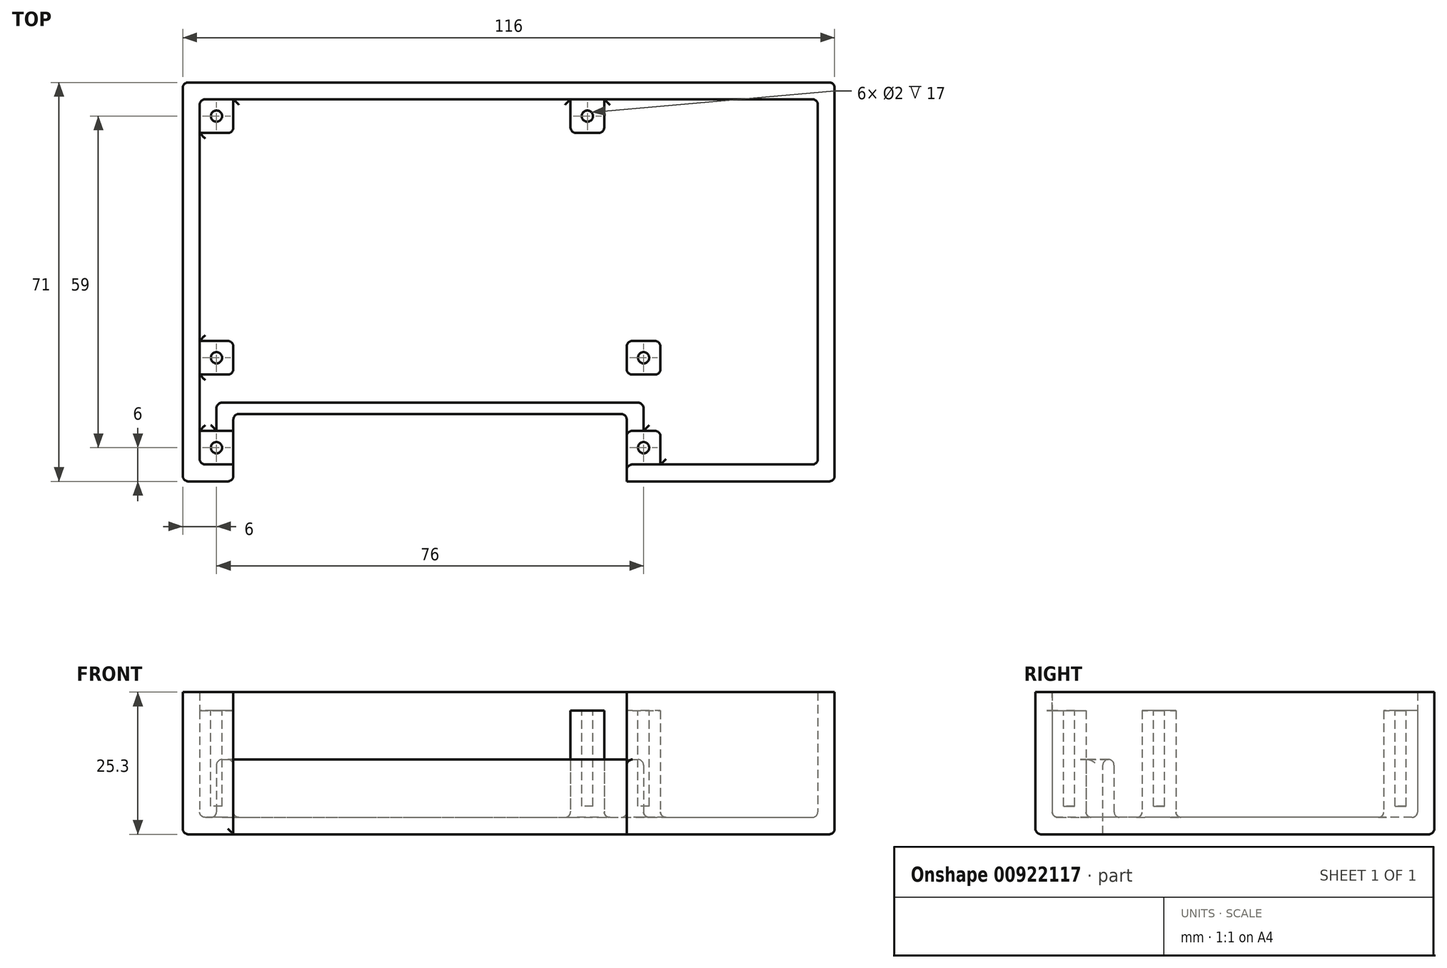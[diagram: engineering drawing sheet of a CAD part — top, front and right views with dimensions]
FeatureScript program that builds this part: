
annotation { "Feature Type Name" : "Feature", "Feature Type Description" : "" }
export const myFeature = defineFeature(function(context is Context, id is Id, definition is map)
    precondition{}
    {
        {
            var Q0;
            Q0=qCreatedBy(makeId("Top.planeOp"),FACE);
            var sketch = newSketch(context, id + "F0", { "sketchPlane" : qUnion([Q0])});
            skLineSegment(sketch, "E0.bottom", {"start": v(58, -35.5) * mm, "end": v(-58, -35.5) * mm});
            skLineSegment(sketch, "E0.top", {"start": v(58, 35.5) * mm, "end": v(-58, 35.5) * mm});
            skLineSegment(sketch, "E0.left", {"start": v(58, -35.5) * mm, "end": v(58, 35.5) * mm});
            skLineSegment(sketch, "E0.right", {"start": v(-58, -35.5) * mm, "end": v(-58, 35.5) * mm});
            skSolve(sketch);
        }
        {
            var Q0;
            Q0 = qSketchRegion(id + "F0", true);
            extrude(context, id + "F1", {"entities" : qUnion([Q0]), "depth" : 3 * mm, "offsetDistance" : 25 * mm});
        }
        {
            var Q0;
            Q0=makeQuery(id+"F1.opExtrude","CAP_FACE",FACE,{"disambiguationData":[OSD([sQuery(id+"F0.wireOp",EDGE,"E0.bottom"),sQuery(id+"F0.wireOp",EDGE,"E0.top"),sQuery(id+"F0.wireOp",EDGE,"E0.left"),sQuery(id+"F0.wireOp",EDGE,"E0.right")])],"isStart":false});
            var sketch = newSketch(context, id + "F2", { "sketchPlane" : qUnion([Q0])});
            skLineSegment(sketch, "E1.bottom", {"start": v(-58, 35.5) * mm, "end": v(58, 35.5) * mm});
            skLineSegment(sketch, "E1.top", {"start": v(-58, -35.5) * mm, "end": v(58, -35.5) * mm});
            skLineSegment(sketch, "E1.left", {"start": v(-58, 35.5) * mm, "end": v(-58, -35.5) * mm});
            skLineSegment(sketch, "E1.right", {"start": v(58, 35.5) * mm, "end": v(58, -35.5) * mm});
            skSolve(sketch);
        }
        {
            var Q0;
            Q0 = qSketchRegion(id + "F2", true);
            extrude(context, id + "F3", {"entities" : qUnion([Q0]), "depth" : 22.3 * mm, "offsetDistance" : 25 * mm});
        }
        {
            var Q0;
            Q0=makeQuery(id+"F1.opExtrude","CAP_FACE",FACE,{"disambiguationData":[OSD([sQuery(id+"F0.wireOp",EDGE,"E0.bottom"),sQuery(id+"F0.wireOp",EDGE,"E0.top"),sQuery(id+"F0.wireOp",EDGE,"E0.left"),sQuery(id+"F0.wireOp",EDGE,"E0.right")])],"isStart":false});
            var sketch = newSketch(context, id + "F4", { "sketchPlane" : qUnion([Q0])});
            skLineSegment(sketch, "E2.bottom", {"start": v(-55, 32.5) * mm, "end": v(55, 32.5) * mm});
            skLineSegment(sketch, "E2.top", {"start": v(-55, -32.5) * mm, "end": v(55, -32.5) * mm});
            skLineSegment(sketch, "E2.left", {"start": v(-55, 32.5) * mm, "end": v(-55, -32.5) * mm});
            skLineSegment(sketch, "E2.right", {"start": v(55, 32.5) * mm, "end": v(55, -32.5) * mm});
            skSolve(sketch);
        }
        {
            var Q0;
            Q0 = qSketchRegion(id + "F4", true);
            extrude(context, id + "F5", {"entities" : qUnion([Q0]), "operationType" : NewBodyOperationType.REMOVE, "depth" : 23 * mm, "offsetDistance" : 25 * mm});
        }
        {
            var Q0;
            Q0=makeQuery(id+"F1.opExtrude","CAP_FACE",FACE,{"disambiguationData":[OSD([sQuery(id+"F0.wireOp",EDGE,"E0.bottom"),sQuery(id+"F0.wireOp",EDGE,"E0.top"),sQuery(id+"F0.wireOp",EDGE,"E0.left"),sQuery(id+"F0.wireOp",EDGE,"E0.right")])],"isStart":false});
            var sketch = newSketch(context, id + "F6", { "sketchPlane" : qUnion([Q0])});
            skLineSegment(sketch, "E3", {"start": v(3.6, 8.06) * mm, "end": v(5.25, 13.83) * mm, "construction": true});
            skLineSegment(sketch, "E4.bottom", {"start": v(-55, -32.5) * mm, "end": v(-49, -32.5) * mm});
            skLineSegment(sketch, "E4.top", {"start": v(-55, -26.5) * mm, "end": v(-49, -26.5) * mm});
            skLineSegment(sketch, "E4.left", {"start": v(-55, -32.5) * mm, "end": v(-55, -26.5) * mm});
            skLineSegment(sketch, "E4.right", {"start": v(-49, -32.5) * mm, "end": v(-49, -26.5) * mm});
            skLineSegment(sketch, "E5.bottom", {"start": v(21, -32.5) * mm, "end": v(27, -32.5) * mm});
            skLineSegment(sketch, "E5.top", {"start": v(21, -26.5) * mm, "end": v(27, -26.5) * mm});
            skLineSegment(sketch, "E5.left", {"start": v(21, -32.5) * mm, "end": v(21, -26.5) * mm});
            skLineSegment(sketch, "E5.right", {"start": v(27, -32.5) * mm, "end": v(27, -26.5) * mm});
            skLineSegment(sketch, "E6.bottom", {"start": v(-49, -10.5) * mm, "end": v(-55, -10.5) * mm});
            skLineSegment(sketch, "E6.top", {"start": v(-49, -16.5) * mm, "end": v(-55, -16.5) * mm});
            skLineSegment(sketch, "E6.left", {"start": v(-49, -10.5) * mm, "end": v(-49, -16.5) * mm});
            skLineSegment(sketch, "E6.right", {"start": v(-55, -10.5) * mm, "end": v(-55, -16.5) * mm});
            skLineSegment(sketch, "E7.bottom", {"start": v(27, -10.5) * mm, "end": v(21, -10.5) * mm});
            skLineSegment(sketch, "E7.top", {"start": v(27, -16.5) * mm, "end": v(21, -16.5) * mm});
            skLineSegment(sketch, "E7.left", {"start": v(27, -10.5) * mm, "end": v(27, -16.5) * mm});
            skLineSegment(sketch, "E7.right", {"start": v(21, -10.5) * mm, "end": v(21, -16.5) * mm});
            skLineSegment(sketch, "E8", {"start": v(21, -10.5) * mm, "end": v(27, -16.5) * mm, "construction": true});
            skPoint(sketch, "E9", {"position": v(24, -13.5) * mm});
            skLineSegment(sketch, "E10", {"start": v(27, -26.5) * mm, "end": v(21, -32.5) * mm, "construction": true});
            skLineSegment(sketch, "E11", {"start": v(-49, -16.5) * mm, "end": v(-55, -10.5) * mm, "construction": true});
            skLineSegment(sketch, "E12", {"start": v(-55, -32.5) * mm, "end": v(-49, -26.5) * mm, "construction": true});
            skPoint(sketch, "E13", {"position": v(-52, -13.5) * mm});
            skPoint(sketch, "E14", {"position": v(-52, -29.5) * mm});
            skPoint(sketch, "E15", {"position": v(24, -29.5) * mm});
            skLineSegment(sketch, "E16", {"start": v(24, -13.5) * mm, "end": v(24, -29.5) * mm, "construction": true});
            skLineSegment(sketch, "E17", {"start": v(24, -13.5) * mm, "end": v(-52, -13.5) * mm, "construction": true});
            skLineSegment(sketch, "E18.bottom", {"start": v(17, 32.5) * mm, "end": v(11, 32.5) * mm});
            skLineSegment(sketch, "E18.top", {"start": v(17, 26.5) * mm, "end": v(11, 26.5) * mm});
            skLineSegment(sketch, "E18.left", {"start": v(17, 32.5) * mm, "end": v(17, 26.5) * mm});
            skLineSegment(sketch, "E18.right", {"start": v(11, 32.5) * mm, "end": v(11, 26.5) * mm});
            skLineSegment(sketch, "E19.bottom", {"start": v(-49, 32.5) * mm, "end": v(-55, 32.5) * mm});
            skLineSegment(sketch, "E19.top", {"start": v(-49, 26.5) * mm, "end": v(-55, 26.5) * mm});
            skLineSegment(sketch, "E19.left", {"start": v(-49, 32.5) * mm, "end": v(-49, 26.5) * mm});
            skLineSegment(sketch, "E19.right", {"start": v(-55, 32.5) * mm, "end": v(-55, 26.5) * mm});
            skLineSegment(sketch, "E20", {"start": v(17, 32.5) * mm, "end": v(11, 26.5) * mm, "construction": true});
            skLineSegment(sketch, "E21", {"start": v(-49, 32.5) * mm, "end": v(-55, 26.5) * mm, "construction": true});
            skPoint(sketch, "E22", {"position": v(-52, 29.5) * mm});
            skPoint(sketch, "E23", {"position": v(14, 29.5) * mm});
            skSolve(sketch);
        }
        {
            var Q0;
            Q0 = qSketchRegion(id + "F6", true);
            extrude(context, id + "F7", {"entities" : qUnion([Q0]), "depth" : 19 * mm, "offsetDistance" : 25 * mm});
        }
        {
            var Q0;
            Q0=makeQuery(id+"F3.opExtrude","CAP_FACE",FACE,{"disambiguationData":[OSD([sQuery(id+"F2.wireOp",EDGE,"E1.bottom"),sQuery(id+"F2.wireOp",EDGE,"E1.top"),sQuery(id+"F2.wireOp",EDGE,"E1.left"),sQuery(id+"F2.wireOp",EDGE,"E1.right")])],"isStart":false});
            var sketch = newSketch(context, id + "F8", { "sketchPlane" : qUnion([Q0])});
            skLineSegment(sketch, "E24.bottom", {"start": v(21, -35.5) * mm, "end": v(-49, -35.5) * mm});
            skLineSegment(sketch, "E24.top", {"start": v(21, -32.5) * mm, "end": v(-49, -32.5) * mm});
            skLineSegment(sketch, "E24.left", {"start": v(21, -35.5) * mm, "end": v(21, -32.5) * mm});
            skLineSegment(sketch, "E24.right", {"start": v(-49, -35.5) * mm, "end": v(-49, -32.5) * mm});
            skSolve(sketch);
        }
        {
            var Q0;
            Q0 = qSketchRegion(id + "F8", true);
            extrude(context, id + "F9", {"entities" : qUnion([Q0]), "operationType" : NewBodyOperationType.REMOVE, "oppositeDirection" : true, "depth" : 24 * mm, "offsetDistance" : 25 * mm});
        }
        {
            var Q0;
            Q0=makeQuery(id+"F7.opExtrude","CAP_FACE",FACE,{"disambiguationData":[OSD([sQuery(id+"F6.wireOp",EDGE,"E4.bottom"),sQuery(id+"F6.wireOp",EDGE,"E4.top"),sQuery(id+"F6.wireOp",EDGE,"E4.left"),sQuery(id+"F6.wireOp",EDGE,"E4.right")])],"isStart":false});
            var sketch = newSketch(context, id + "F10", { "sketchPlane" : qUnion([Q0])});
            skCircle(sketch, "E25", {"center": v(-52, -29.5) * mm, "radius": 1 * mm});
            skCircle(sketch, "E26", {"center": v(-52, -13.5) * mm, "radius": 1 * mm});
            skCircle(sketch, "E27", {"center": v(-52, 29.5) * mm, "radius": 1 * mm});
            skCircle(sketch, "E28", {"center": v(14, 29.5) * mm, "radius": 1 * mm});
            skCircle(sketch, "E29", {"center": v(24, -13.5) * mm, "radius": 1 * mm});
            skCircle(sketch, "E30", {"center": v(24, -29.5) * mm, "radius": 1 * mm});
            skSolve(sketch);
        }
        {
            var Q0;
            Q0 = qSketchRegion(id + "F10", true);
            extrude(context, id + "F11", {"entities" : qUnion([Q0]), "operationType" : NewBodyOperationType.REMOVE, "oppositeDirection" : true, "depth" : 17 * mm, "offsetDistance" : 25 * mm});
        }
        {
            var Q0;
            Q0=makeQuery(id+"F1.opExtrude","CAP_FACE",FACE,{"disambiguationData":[OSD([sQuery(id+"F0.wireOp",EDGE,"E0.bottom"),sQuery(id+"F0.wireOp",EDGE,"E0.top"),sQuery(id+"F0.wireOp",EDGE,"E0.left"),sQuery(id+"F0.wireOp",EDGE,"E0.right")])],"isStart":false});
            var sketch = newSketch(context, id + "F12", { "sketchPlane" : qUnion([Q0])});
            skLineSegment(sketch, "E31.bottom", {"start": v(-52, -21.5) * mm, "end": v(24, -21.5) * mm});
            skLineSegment(sketch, "E31.top", {"start": v(-52, -26.5) * mm, "end": v(24, -26.5) * mm});
            skLineSegment(sketch, "E31.left", {"start": v(-52, -21.5) * mm, "end": v(-52, -26.5) * mm});
            skLineSegment(sketch, "E31.right", {"start": v(24, -21.5) * mm, "end": v(24, -26.5) * mm});
            skSolve(sketch);
        }
        {
            var Q0;
            Q0 = qSketchRegion(id + "F12", true);
            extrude(context, id + "F13", {"entities" : qUnion([Q0]), "depth" : 10.3 * mm, "offsetDistance" : 25 * mm});
        }
        {
            var Q0;
            Q0=makeQuery(id+"F1.opExtrude","CAP_FACE",FACE,{"disambiguationData":[OSD([sQuery(id+"F0.wireOp",EDGE,"E0.bottom"),sQuery(id+"F0.wireOp",EDGE,"E0.top"),sQuery(id+"F0.wireOp",EDGE,"E0.left"),sQuery(id+"F0.wireOp",EDGE,"E0.right")])],"isStart":false});
            var sketch = newSketch(context, id + "F14", { "sketchPlane" : qUnion([Q0])});
            skLineSegment(sketch, "E32.bottom", {"start": v(-49, -35.5) * mm, "end": v(21, -35.5) * mm});
            skLineSegment(sketch, "E32.top", {"start": v(-49, -23.5) * mm, "end": v(21, -23.5) * mm});
            skLineSegment(sketch, "E32.left", {"start": v(-49, -35.5) * mm, "end": v(-49, -23.5) * mm});
            skLineSegment(sketch, "E32.right", {"start": v(21, -35.5) * mm, "end": v(21, -23.5) * mm});
            skLineSegment(sketch, "E33", {"start": v(-52, -29.5) * mm, "end": v(24, -29.5) * mm, "construction": true});
            skSolve(sketch);
        }
        {
            var Q0;
            Q0 = qSketchRegion(id + "F14", true);
            extrude(context, id + "F15", {"entities" : qUnion([Q0]), "operationType" : NewBodyOperationType.REMOVE, "oppositeDirection" : true, "depth" : 3 * mm, "offsetDistance" : 25 * mm, "hasSecondDirection" : true, "secondDirectionOppositeDirection" : false, "secondDirectionDepth" : 11.3 * mm});
        }
        {
            var Q0;
            Q0=makeQuery(id+"F3.opExtrude","SWEPT_BODY",BODY,{"disambiguationData":[OSD([sQuery(id+"F2.wireOp",EDGE,"E1.bottom"),sQuery(id+"F2.wireOp",EDGE,"E1.top"),sQuery(id+"F2.wireOp",EDGE,"E1.left"),sQuery(id+"F2.wireOp",EDGE,"E1.right")])]});
            var Q1;
            Q1=makeQuery(id+"F7.opExtrude","SWEPT_BODY",BODY,{"disambiguationData":[OSD([sQuery(id+"F6.wireOp",EDGE,"E4.bottom"),sQuery(id+"F6.wireOp",EDGE,"E4.top"),sQuery(id+"F6.wireOp",EDGE,"E4.left"),sQuery(id+"F6.wireOp",EDGE,"E4.right")])]});
            var Q2;
            Q2=makeQuery(id+"F7.opExtrude","SWEPT_BODY",BODY,{"disambiguationData":[OSD([sQuery(id+"F6.wireOp",EDGE,"E5.bottom"),sQuery(id+"F6.wireOp",EDGE,"E5.top"),sQuery(id+"F6.wireOp",EDGE,"E5.left"),sQuery(id+"F6.wireOp",EDGE,"E5.right")])]});
            var Q3;
            Q3=makeQuery(id+"F7.opExtrude","SWEPT_BODY",BODY,{"disambiguationData":[OSD([sQuery(id+"F6.wireOp",EDGE,"E6.bottom"),sQuery(id+"F6.wireOp",EDGE,"E6.top"),sQuery(id+"F6.wireOp",EDGE,"E6.left"),sQuery(id+"F6.wireOp",EDGE,"E6.right")])]});
            var Q4;
            Q4=makeQuery(id+"F7.opExtrude","SWEPT_BODY",BODY,{"disambiguationData":[OSD([sQuery(id+"F6.wireOp",EDGE,"E7.bottom"),sQuery(id+"F6.wireOp",EDGE,"E7.top"),sQuery(id+"F6.wireOp",EDGE,"E7.left"),sQuery(id+"F6.wireOp",EDGE,"E7.right")])]});
            var Q5;
            Q5=makeQuery(id+"F7.opExtrude","SWEPT_BODY",BODY,{"disambiguationData":[OSD([sQuery(id+"F6.wireOp",EDGE,"E18.bottom"),sQuery(id+"F6.wireOp",EDGE,"E18.top"),sQuery(id+"F6.wireOp",EDGE,"E18.left"),sQuery(id+"F6.wireOp",EDGE,"E18.right")])]});
            var Q6;
            Q6=makeQuery(id+"F7.opExtrude","SWEPT_BODY",BODY,{"disambiguationData":[OSD([sQuery(id+"F6.wireOp",EDGE,"E19.bottom"),sQuery(id+"F6.wireOp",EDGE,"E19.top"),sQuery(id+"F6.wireOp",EDGE,"E19.left"),sQuery(id+"F6.wireOp",EDGE,"E19.right")])]});
            var Q7;
            Q7=makeQuery(id+"F13.opExtrude","SWEPT_BODY",BODY,{"disambiguationData":[OSD([sQuery(id+"F12.wireOp",EDGE,"E31.bottom"),sQuery(id+"F12.wireOp",EDGE,"E31.top"),sQuery(id+"F12.wireOp",EDGE,"E31.left"),sQuery(id+"F12.wireOp",EDGE,"E31.right")])]});
            var Q8;
            Q8=makeQuery(id+"F1.opExtrude","SWEPT_BODY",BODY,{"disambiguationData":[OSD([sQuery(id+"F0.wireOp",EDGE,"E0.bottom"),sQuery(id+"F0.wireOp",EDGE,"E0.top"),sQuery(id+"F0.wireOp",EDGE,"E0.left"),sQuery(id+"F0.wireOp",EDGE,"E0.right")])]});
            booleanBodies(context, id + "F16", {"operationType" : BooleanOperationType.UNION, "tools" : qUnion([Q0, Q1, Q2, Q3, Q4, Q5, Q6, Q7, Q8])});
        }
        {
            var Q0;
            Q0=makeQuery(id+"F16.opBoolean","MERGE",EDGE,{"derivedFrom":[makeQuery(id+"F1.opExtrude","SWEPT_EDGE",EDGE,{"disambiguationData":[OSD([sQuery(id+"F0.wireOp",EDGE,"E0.bottom"),sQuery(id+"F0.wireOp",EDGE,"E0.right")])]}),makeQuery(id+"F3.opExtrude","SWEPT_EDGE",EDGE,{"disambiguationData":[OSD([sQuery(id+"F2.wireOp",EDGE,"E1.top"),sQuery(id+"F2.wireOp",EDGE,"E1.left")])]})]});
            var Q1;
            Q1=makeQuery(id+"F1.opExtrude","CAP_EDGE",EDGE,{"disambiguationData":[OSD([sQuery(id+"F0.wireOp",EDGE,"E0.right")])],"isStart":true});
            var Q2;
            Q2=makeQuery(id+"F16.opBoolean","MERGE",EDGE,{"derivedFrom":[makeQuery(id+"F1.opExtrude","SWEPT_EDGE",EDGE,{"disambiguationData":[OSD([sQuery(id+"F0.wireOp",EDGE,"E0.top"),sQuery(id+"F0.wireOp",EDGE,"E0.right")])]}),makeQuery(id+"F3.opExtrude","SWEPT_EDGE",EDGE,{"disambiguationData":[OSD([sQuery(id+"F2.wireOp",EDGE,"E1.bottom"),sQuery(id+"F2.wireOp",EDGE,"E1.left")])]})]});
            var Q3;
            Q3=makeQuery(id+"F1.opExtrude","CAP_EDGE",EDGE,{"disambiguationData":[OSD([sQuery(id+"F0.wireOp",EDGE,"E0.top")])],"isStart":true});
            var Q4;
            Q4=makeQuery(id+"F16.opBoolean","MERGE",EDGE,{"derivedFrom":[makeQuery(id+"F1.opExtrude","SWEPT_EDGE",EDGE,{"disambiguationData":[OSD([sQuery(id+"F0.wireOp",EDGE,"E0.top"),sQuery(id+"F0.wireOp",EDGE,"E0.left")])]}),makeQuery(id+"F3.opExtrude","SWEPT_EDGE",EDGE,{"disambiguationData":[OSD([sQuery(id+"F2.wireOp",EDGE,"E1.bottom"),sQuery(id+"F2.wireOp",EDGE,"E1.right")])]})]});
            var Q5;
            Q5=makeQuery(id+"F1.opExtrude","CAP_EDGE",EDGE,{"disambiguationData":[OSD([sQuery(id+"F0.wireOp",EDGE,"E0.left")])],"isStart":true});
            var Q6;
            Q6=makeQuery(id+"F16.opBoolean","MERGE",EDGE,{"derivedFrom":[makeQuery(id+"F1.opExtrude","SWEPT_EDGE",EDGE,{"disambiguationData":[OSD([sQuery(id+"F0.wireOp",EDGE,"E0.bottom"),sQuery(id+"F0.wireOp",EDGE,"E0.left")])]}),makeQuery(id+"F3.opExtrude","SWEPT_EDGE",EDGE,{"disambiguationData":[OSD([sQuery(id+"F2.wireOp",EDGE,"E1.top"),sQuery(id+"F2.wireOp",EDGE,"E1.right")])]})]});
            var Q7;
            {var subQ0=sQuery(id+"F0.wireOp",EDGE,"E0.bottom");var subQ5=sQuery(id+"F0.wireOp",EDGE,"E0.left");Q7=makeQuery(id+"F15.boolean.opBoolean","SPLIT",EDGE,{"disambiguationData":[TD([makeQuery(id+"F1.opExtrude","SWEPT_FACE",FACE,{"disambiguationData":[OSD([subQ5])]})])],"derivedFrom":makeQuery(id+"F1.opExtrude","CAP_EDGE",EDGE,{"disambiguationData":[OSD([subQ0])],"isStart":true})});}
            var Q8;
            {var subQ0=sQuery(id+"F2.wireOp",EDGE,"E1.top");var subQ1=sQuery(id+"F8.wireOp",EDGE,"E24.left");var subQ3=makeQuery(id+"F9.opExtrude","SWEPT_EDGE",EDGE,{"disambiguationData":[OSD([subQ0,sQuery(id+"F8.wireOp",EDGE,"E24.bottom"),subQ1])]});var subQ4=sQuery(id+"F0.wireOp",EDGE,"E0.bottom");Q8=makeQuery(id+"F16.opBoolean","MERGE",EDGE,{"derivedFrom":[makeQuery(id+"F15.boolean.opBoolean","MERGE",EDGE,{"derivedFrom":[makeQuery(id+"F9.boolean.opBoolean","COPY",EDGE,{"disambiguationData":[topologyDisambiguationEdgeConnected([makeQuery(id+"F1.opExtrude","SWEPT_FACE",FACE,{"disambiguationData":[OSD([subQ4])]})])],"derivedFrom":subQ3})],"fromTools":[makeQuery(id+"F15.opExtrude","SWEPT_EDGE",EDGE,{"disambiguationData":[OSD([subQ4,sQuery(id+"F14.wireOp",EDGE,"E32.bottom"),sQuery(id+"F14.wireOp",EDGE,"E32.right")])]})]}),makeQuery(id+"F9.boolean.opBoolean","COPY",EDGE,{"disambiguationData":[topologyDisambiguationEdgeConnected([makeQuery(id+"F3.opExtrude","SWEPT_FACE",FACE,{"disambiguationData":[OSD([subQ0])]})])],"derivedFrom":subQ3})]});}
            var Q9;
            Q9=makeQuery(id+"F15.boolean.opBoolean","COPY",EDGE,{"derivedFrom":makeQuery(id+"F15.opExtrude","CAP_EDGE",EDGE,{"disambiguationData":[OSD([sQuery(id+"F14.wireOp",EDGE,"E32.right")])],"isStart":false})});
            var Q10;
            Q10=makeQuery(id+"F15.boolean.opBoolean","COPY",EDGE,{"derivedFrom":makeQuery(id+"F15.opExtrude","CAP_EDGE",EDGE,{"disambiguationData":[OSD([sQuery(id+"F14.wireOp",EDGE,"E32.top")])],"isStart":false})});
            var Q11;
            {var subQ0=sQuery(id+"F2.wireOp",EDGE,"E1.top");var subQ1=sQuery(id+"F8.wireOp",EDGE,"E24.right");var subQ3=makeQuery(id+"F9.opExtrude","SWEPT_EDGE",EDGE,{"disambiguationData":[OSD([subQ0,sQuery(id+"F8.wireOp",EDGE,"E24.bottom"),subQ1])]});var subQ4=sQuery(id+"F0.wireOp",EDGE,"E0.bottom");Q11=makeQuery(id+"F16.opBoolean","MERGE",EDGE,{"derivedFrom":[makeQuery(id+"F15.boolean.opBoolean","MERGE",EDGE,{"derivedFrom":[makeQuery(id+"F9.boolean.opBoolean","COPY",EDGE,{"disambiguationData":[topologyDisambiguationEdgeConnected([makeQuery(id+"F1.opExtrude","SWEPT_FACE",FACE,{"disambiguationData":[OSD([subQ4])]})])],"derivedFrom":subQ3})],"fromTools":[makeQuery(id+"F15.opExtrude","SWEPT_EDGE",EDGE,{"disambiguationData":[OSD([subQ4,sQuery(id+"F14.wireOp",EDGE,"E32.bottom"),sQuery(id+"F14.wireOp",EDGE,"E32.left")])]})]}),makeQuery(id+"F9.boolean.opBoolean","COPY",EDGE,{"disambiguationData":[topologyDisambiguationEdgeConnected([makeQuery(id+"F3.opExtrude","SWEPT_FACE",FACE,{"disambiguationData":[OSD([subQ0])]})])],"derivedFrom":subQ3})]});}
            var Q12;
            {var subQ0=sQuery(id+"F0.wireOp",EDGE,"E0.bottom");var subQ4=sQuery(id+"F0.wireOp",EDGE,"E0.right");Q12=makeQuery(id+"F15.boolean.opBoolean","SPLIT",EDGE,{"disambiguationData":[TD([makeQuery(id+"F1.opExtrude","SWEPT_FACE",FACE,{"disambiguationData":[OSD([subQ4])]})])],"derivedFrom":makeQuery(id+"F1.opExtrude","CAP_EDGE",EDGE,{"disambiguationData":[OSD([subQ0])],"isStart":true})});}
            var Q13;
            {var subQ0=sQuery(id+"F14.wireOp",EDGE,"E32.top");var subQ1=makeQuery(id+"F15.opExtrude","SWEPT_FACE",FACE,{"disambiguationData":[OSD([subQ0])]});var subQ2=sQuery(id+"F14.wireOp",EDGE,"E32.right");var subQ3=makeQuery(id+"F15.opExtrude","SWEPT_FACE",FACE,{"disambiguationData":[OSD([subQ2])]});var subQ4=makeQuery(id+"F15.opExtrude","SWEPT_EDGE",EDGE,{"disambiguationData":[OSD([subQ0,subQ2])]});var subQ5=sQuery(id+"F0.wireOp",EDGE,"E0.bottom");var subQ6=sQuery(id+"F8.wireOp",EDGE,"E24.left");Q13=makeQuery(id+"F16.opBoolean","MERGE",EDGE,{"derivedFrom":[makeQuery(id+"F15.boolean.opBoolean","COPY",EDGE,{"disambiguationData":[topologyDisambiguationEdgeConnected([makeQuery(id+"F9.boolean.opBoolean","COPY",FACE,{"disambiguationData":[TD([makeQuery(id+"F1.opExtrude","SWEPT_FACE",FACE,{"disambiguationData":[OSD([subQ5])]})])],"derivedFrom":makeQuery(id+"F9.opExtrude","SWEPT_FACE",FACE,{"disambiguationData":[OSD([subQ6])]})}),subQ1,subQ3])],"derivedFrom":subQ4}),makeQuery(id+"F15.boolean.opBoolean","COPY",EDGE,{"disambiguationData":[topologyDisambiguationEdgeConnected([subQ1,subQ3])],"derivedFrom":subQ4})]});}
            var Q14;
            {var subQ0=sQuery(id+"F14.wireOp",EDGE,"E32.top");var subQ1=makeQuery(id+"F15.opExtrude","SWEPT_FACE",FACE,{"disambiguationData":[OSD([subQ0])]});var subQ2=sQuery(id+"F14.wireOp",EDGE,"E32.left");var subQ3=makeQuery(id+"F15.opExtrude","SWEPT_FACE",FACE,{"disambiguationData":[OSD([subQ2])]});var subQ4=makeQuery(id+"F15.opExtrude","SWEPT_EDGE",EDGE,{"disambiguationData":[OSD([subQ0,subQ2])]});var subQ5=sQuery(id+"F0.wireOp",EDGE,"E0.bottom");var subQ6=sQuery(id+"F8.wireOp",EDGE,"E24.right");Q14=makeQuery(id+"F16.opBoolean","MERGE",EDGE,{"derivedFrom":[makeQuery(id+"F15.boolean.opBoolean","COPY",EDGE,{"disambiguationData":[topologyDisambiguationEdgeConnected([makeQuery(id+"F9.boolean.opBoolean","COPY",FACE,{"disambiguationData":[TD([makeQuery(id+"F1.opExtrude","SWEPT_FACE",FACE,{"disambiguationData":[OSD([subQ5])]})])],"derivedFrom":makeQuery(id+"F9.opExtrude","SWEPT_FACE",FACE,{"disambiguationData":[OSD([subQ6])]})}),subQ1,subQ3])],"derivedFrom":subQ4}),makeQuery(id+"F15.boolean.opBoolean","COPY",EDGE,{"disambiguationData":[topologyDisambiguationEdgeConnected([subQ1,subQ3])],"derivedFrom":subQ4})]});}
            var Q15;
            Q15=makeQuery(id+"F15.boolean.opBoolean","COPY",EDGE,{"derivedFrom":makeQuery(id+"F15.opExtrude","CAP_EDGE",EDGE,{"disambiguationData":[OSD([sQuery(id+"F14.wireOp",EDGE,"E32.left")])],"isStart":false})});
            var Q16;
            Q16=makeQuery(id+"F15.boolean.opBoolean","INTERSECT",EDGE,{"derivedFrom":[makeQuery(id+"F13.opExtrude","CAP_FACE",FACE,{"disambiguationData":[OSD([sQuery(id+"F12.wireOp",EDGE,"E31.bottom"),sQuery(id+"F12.wireOp",EDGE,"E31.top"),sQuery(id+"F12.wireOp",EDGE,"E31.left"),sQuery(id+"F12.wireOp",EDGE,"E31.right")])],"isStart":false}),makeQuery(id+"F15.opExtrude","SWEPT_FACE",FACE,{"disambiguationData":[OSD([sQuery(id+"F14.wireOp",EDGE,"E32.left")])]})]});
            var Q17;
            Q17=makeQuery(id+"F13.opExtrude","CAP_EDGE",EDGE,{"disambiguationData":[OSD([sQuery(id+"F12.wireOp",EDGE,"E31.left")])],"isStart":false});
            var Q18;
            Q18=makeQuery(id+"F13.opExtrude","CAP_EDGE",EDGE,{"disambiguationData":[OSD([sQuery(id+"F12.wireOp",EDGE,"E31.bottom")])],"isStart":false});
            var Q19;
            Q19=makeQuery(id+"F15.boolean.opBoolean","INTERSECT",EDGE,{"derivedFrom":[makeQuery(id+"F13.opExtrude","CAP_FACE",FACE,{"disambiguationData":[OSD([sQuery(id+"F12.wireOp",EDGE,"E31.bottom"),sQuery(id+"F12.wireOp",EDGE,"E31.top"),sQuery(id+"F12.wireOp",EDGE,"E31.left"),sQuery(id+"F12.wireOp",EDGE,"E31.right")])],"isStart":false}),makeQuery(id+"F15.opExtrude","SWEPT_FACE",FACE,{"disambiguationData":[OSD([sQuery(id+"F14.wireOp",EDGE,"E32.top")])]})]});
            var Q20;
            Q20=makeQuery(id+"F13.opExtrude","CAP_EDGE",EDGE,{"disambiguationData":[OSD([sQuery(id+"F12.wireOp",EDGE,"E31.right")])],"isStart":false});
            var Q21;
            Q21=makeQuery(id+"F1.opExtrude","CAP_FACE",FACE,{"disambiguationData":[OSD([sQuery(id+"F0.wireOp",EDGE,"E0.bottom"),sQuery(id+"F0.wireOp",EDGE,"E0.top"),sQuery(id+"F0.wireOp",EDGE,"E0.left"),sQuery(id+"F0.wireOp",EDGE,"E0.right")])],"isStart":false});
            var Q22;
            Q22=makeQuery(id+"F7.opExtrude","SWEPT_EDGE",EDGE,{"disambiguationData":[OSD([sQuery(id+"F6.wireOp",EDGE,"E18.bottom"),sQuery(id+"F6.wireOp",EDGE,"E18.right")])]});
            var Q23;
            Q23=makeQuery(id+"F7.opExtrude","SWEPT_EDGE",EDGE,{"disambiguationData":[OSD([sQuery(id+"F6.wireOp",EDGE,"E18.top"),sQuery(id+"F6.wireOp",EDGE,"E18.right")])]});
            var Q24;
            Q24=makeQuery(id+"F7.opExtrude","SWEPT_EDGE",EDGE,{"disambiguationData":[OSD([sQuery(id+"F6.wireOp",EDGE,"E18.top"),sQuery(id+"F6.wireOp",EDGE,"E18.left")])]});
            var Q25;
            Q25=makeQuery(id+"F7.opExtrude","SWEPT_EDGE",EDGE,{"disambiguationData":[OSD([sQuery(id+"F6.wireOp",EDGE,"E18.bottom"),sQuery(id+"F6.wireOp",EDGE,"E18.left")])]});
            var Q26;
            Q26=makeQuery(id+"F7.opExtrude","SWEPT_EDGE",EDGE,{"disambiguationData":[OSD([sQuery(id+"F6.wireOp",EDGE,"E7.bottom"),sQuery(id+"F6.wireOp",EDGE,"E7.left")])]});
            var Q27;
            Q27=makeQuery(id+"F7.opExtrude","SWEPT_EDGE",EDGE,{"disambiguationData":[OSD([sQuery(id+"F6.wireOp",EDGE,"E7.top"),sQuery(id+"F6.wireOp",EDGE,"E7.left")])]});
            var Q28;
            Q28=makeQuery(id+"F7.opExtrude","SWEPT_EDGE",EDGE,{"disambiguationData":[OSD([sQuery(id+"F6.wireOp",EDGE,"E7.top"),sQuery(id+"F6.wireOp",EDGE,"E7.right")])]});
            var Q29;
            Q29=makeQuery(id+"F7.opExtrude","SWEPT_EDGE",EDGE,{"disambiguationData":[OSD([sQuery(id+"F6.wireOp",EDGE,"E7.bottom"),sQuery(id+"F6.wireOp",EDGE,"E7.right")])]});
            var Q30;
            Q30=makeQuery(id+"F7.opExtrude","SWEPT_EDGE",EDGE,{"disambiguationData":[OSD([sQuery(id+"F6.wireOp",EDGE,"E19.bottom"),sQuery(id+"F6.wireOp",EDGE,"E19.left")])]});
            var Q31;
            Q31=makeQuery(id+"F7.opExtrude","SWEPT_EDGE",EDGE,{"disambiguationData":[OSD([sQuery(id+"F6.wireOp",EDGE,"E19.top"),sQuery(id+"F6.wireOp",EDGE,"E19.left")])]});
            var Q32;
            Q32=makeQuery(id+"F7.opExtrude","SWEPT_EDGE",EDGE,{"disambiguationData":[OSD([sQuery(id+"F6.wireOp",EDGE,"E19.top"),sQuery(id+"F6.wireOp",EDGE,"E19.right")])]});
            var Q33;
            Q33=makeQuery(id+"F7.opExtrude","SWEPT_EDGE",EDGE,{"disambiguationData":[OSD([sQuery(id+"F6.wireOp",EDGE,"E5.top"),sQuery(id+"F6.wireOp",EDGE,"E5.left")])]});
            var Q34;
            {var subQ0=sQuery(id+"F4.wireOp",EDGE,"E2.top");var subQ1=sQuery(id+"F8.wireOp",EDGE,"E24.left");Q34=makeQuery(id+"F9.boolean.opBoolean","COPY",EDGE,{"disambiguationData":[topologyDisambiguationEdgeConnected([makeQuery(id+"F5.boolean.opBoolean","COPY",FACE,{"derivedFrom":makeQuery(id+"F5.opExtrude","SWEPT_FACE",FACE,{"disambiguationData":[OSD([subQ0])]})})])],"derivedFrom":makeQuery(id+"F9.opExtrude","SWEPT_EDGE",EDGE,{"disambiguationData":[OSD([sQuery(id+"F2.wireOp",EDGE,"E1.bottom"),sQuery(id+"F2.wireOp",EDGE,"E1.top"),sQuery(id+"F2.wireOp",EDGE,"E1.left"),sQuery(id+"F2.wireOp",EDGE,"E1.right"),subQ0,sQuery(id+"F8.wireOp",EDGE,"E24.top"),subQ1])]})});}
            var Q35;
            Q35=makeQuery(id+"F7.opExtrude","SWEPT_EDGE",EDGE,{"disambiguationData":[OSD([sQuery(id+"F6.wireOp",EDGE,"E5.top"),sQuery(id+"F6.wireOp",EDGE,"E5.right")])]});
            var Q36;
            Q36=makeQuery(id+"F7.opExtrude","SWEPT_EDGE",EDGE,{"disambiguationData":[OSD([sQuery(id+"F6.wireOp",EDGE,"E5.bottom"),sQuery(id+"F6.wireOp",EDGE,"E5.right")])]});
            var Q37;
            Q37=makeQuery(id+"F13.opExtrude","SWEPT_EDGE",EDGE,{"disambiguationData":[OSD([sQuery(id+"F12.wireOp",EDGE,"E31.bottom"),sQuery(id+"F12.wireOp",EDGE,"E31.right")])]});
            var Q38;
            Q38=makeQuery(id+"F13.opExtrude","SWEPT_EDGE",EDGE,{"disambiguationData":[OSD([sQuery(id+"F12.wireOp",EDGE,"E31.top"),sQuery(id+"F12.wireOp",EDGE,"E31.right")])]});
            var Q39;
            Q39=makeQuery(id+"F13.opExtrude","SWEPT_EDGE",EDGE,{"disambiguationData":[OSD([sQuery(id+"F12.wireOp",EDGE,"E31.bottom"),sQuery(id+"F12.wireOp",EDGE,"E31.left")])]});
            var Q40;
            Q40=makeQuery(id+"F13.opExtrude","SWEPT_EDGE",EDGE,{"disambiguationData":[OSD([sQuery(id+"F12.wireOp",EDGE,"E31.top"),sQuery(id+"F12.wireOp",EDGE,"E31.left")])]});
            var Q41;
            Q41=makeQuery(id+"F7.opExtrude","SWEPT_EDGE",EDGE,{"disambiguationData":[OSD([sQuery(id+"F6.wireOp",EDGE,"E4.top"),sQuery(id+"F6.wireOp",EDGE,"E4.left")])]});
            var Q42;
            Q42=makeQuery(id+"F7.opExtrude","SWEPT_EDGE",EDGE,{"disambiguationData":[OSD([sQuery(id+"F6.wireOp",EDGE,"E6.top"),sQuery(id+"F6.wireOp",EDGE,"E6.right")])]});
            var Q43;
            Q43=makeQuery(id+"F7.opExtrude","SWEPT_EDGE",EDGE,{"disambiguationData":[OSD([sQuery(id+"F6.wireOp",EDGE,"E6.top"),sQuery(id+"F6.wireOp",EDGE,"E6.left")])]});
            var Q44;
            Q44=makeQuery(id+"F7.opExtrude","SWEPT_EDGE",EDGE,{"disambiguationData":[OSD([sQuery(id+"F6.wireOp",EDGE,"E6.bottom"),sQuery(id+"F6.wireOp",EDGE,"E6.left")])]});
            var Q45;
            Q45=makeQuery(id+"F7.opExtrude","SWEPT_EDGE",EDGE,{"disambiguationData":[OSD([sQuery(id+"F6.wireOp",EDGE,"E6.bottom"),sQuery(id+"F6.wireOp",EDGE,"E6.right")])]});
            var Q46;
            Q46=makeQuery(id+"F5.boolean.opBoolean","COPY",EDGE,{"derivedFrom":makeQuery(id+"F5.opExtrude","SWEPT_EDGE",EDGE,{"disambiguationData":[OSD([sQuery(id+"F4.wireOp",EDGE,"E2.bottom"),sQuery(id+"F4.wireOp",EDGE,"E2.left")])]})});
            var Q47;
            Q47=makeQuery(id+"F5.boolean.opBoolean","COPY",EDGE,{"derivedFrom":makeQuery(id+"F5.opExtrude","SWEPT_EDGE",EDGE,{"disambiguationData":[OSD([sQuery(id+"F4.wireOp",EDGE,"E2.top"),sQuery(id+"F4.wireOp",EDGE,"E2.left")])]})});
            var Q48;
            Q48=makeQuery(id+"F5.boolean.opBoolean","COPY",EDGE,{"derivedFrom":makeQuery(id+"F5.opExtrude","SWEPT_EDGE",EDGE,{"disambiguationData":[OSD([sQuery(id+"F4.wireOp",EDGE,"E2.top"),sQuery(id+"F4.wireOp",EDGE,"E2.right")])]})});
            var Q49;
            Q49=makeQuery(id+"F5.boolean.opBoolean","COPY",EDGE,{"derivedFrom":makeQuery(id+"F5.opExtrude","SWEPT_EDGE",EDGE,{"disambiguationData":[OSD([sQuery(id+"F4.wireOp",EDGE,"E2.bottom"),sQuery(id+"F4.wireOp",EDGE,"E2.right")])]})});
            fillet(context, id + "F17", {"entities" : qUnion([Q0, Q1, Q2, Q3, Q4, Q5, Q6, Q7, Q8, Q9, Q10, Q11, Q12, Q13, Q14, Q15, Q16, Q17, Q18, Q19, Q20, Q21, Q22, Q23, Q24, Q25, Q26, Q27, Q28, Q29, Q30, Q31, Q32, Q33, Q34, Q35, Q36, Q37, Q38, Q39, Q40, Q41, Q42, Q43, Q44, Q45, Q46, Q47, Q48, Q49]), "radius" : 1 * mm, "tangentPropagation" : true, "allowEdgeOverflow" : false});
        }
    });
